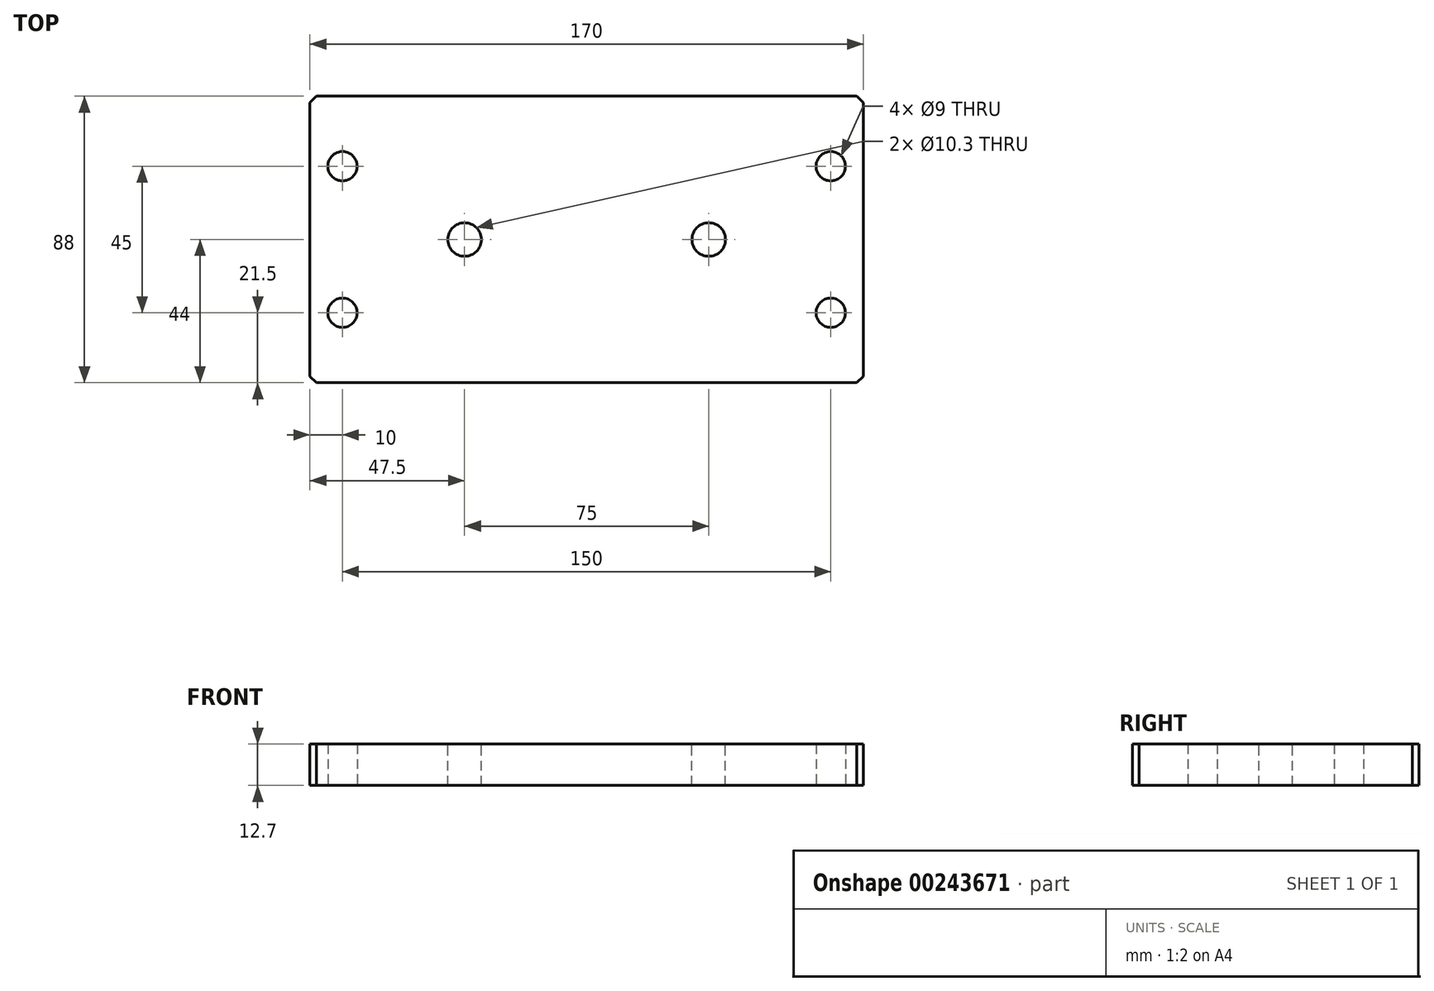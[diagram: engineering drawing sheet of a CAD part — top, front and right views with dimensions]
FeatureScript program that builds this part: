
annotation { "Feature Type Name" : "Feature", "Feature Type Description" : "" }
export const myFeature = defineFeature(function(context is Context, id is Id, definition is map)
    precondition{}
    {
        {
            var Q0;
            Q0=qCreatedBy(makeId("Top.planeOp"),FACE);
            var sketch = newSketch(context, id + "F0", { "sketchPlane" : qUnion([Q0])});
            skLineSegment(sketch, "E0.bottom", {"start": v(-85, -44) * mm, "end": v(85, -44) * mm});
            skLineSegment(sketch, "E0.top", {"start": v(-85, 44) * mm, "end": v(85, 44) * mm});
            skLineSegment(sketch, "E0.left", {"start": v(-85, -44) * mm, "end": v(-85, 44) * mm});
            skLineSegment(sketch, "E0.right", {"start": v(85, -44) * mm, "end": v(85, 44) * mm});
            skPoint(sketch, "E0.middle", {"position": v(0, 0) * mm});
            skLineSegment(sketch, "E1.bottom", {"start": v(-75, -22.5) * mm, "end": v(75, -22.5) * mm, "construction": true});
            skLineSegment(sketch, "E1.top", {"start": v(-75, 22.5) * mm, "end": v(75, 22.5) * mm, "construction": true});
            skLineSegment(sketch, "E1.left", {"start": v(-75, -22.5) * mm, "end": v(-75, 22.5) * mm, "construction": true});
            skLineSegment(sketch, "E1.right", {"start": v(75, -22.5) * mm, "end": v(75, 22.5) * mm, "construction": true});
            skCircle(sketch, "E2", {"center": v(-75, 22.5) * mm, "radius": 4.5 * mm});
            skCircle(sketch, "E3", {"center": v(75, 22.5) * mm, "radius": 4.5 * mm});
            skCircle(sketch, "E4", {"center": v(75, -22.5) * mm, "radius": 4.5 * mm});
            skCircle(sketch, "E5", {"center": v(-75, -22.5) * mm, "radius": 4.5 * mm});
            skSolve(sketch);
        }
        {
            var Q0;
            Q0 = qSketchRegion(id + "F0", true);
            extrude(context, id + "F1", {"entities" : qUnion([Q0]), "endBound" : BoundingType.SYMMETRIC, "depth" : 12.7 * mm});
        }
        {
            var Q0;
            Q0=makeQuery(id+"F1.opExtrude","SWEPT_EDGE",EDGE,{"disambiguationData":[OSD([sQuery(id+"F0.wireOp",EDGE,"E0.top"),sQuery(id+"F0.wireOp",EDGE,"E0.right")])]});
            var Q1;
            Q1=makeQuery(id+"F1.opExtrude","SWEPT_EDGE",EDGE,{"disambiguationData":[OSD([sQuery(id+"F0.wireOp",EDGE,"E0.bottom"),sQuery(id+"F0.wireOp",EDGE,"E0.right")])]});
            var Q2;
            Q2=makeQuery(id+"F1.opExtrude","SWEPT_EDGE",EDGE,{"disambiguationData":[OSD([sQuery(id+"F0.wireOp",EDGE,"E0.top"),sQuery(id+"F0.wireOp",EDGE,"E0.left")])]});
            var Q3;
            Q3=makeQuery(id+"F1.opExtrude","SWEPT_EDGE",EDGE,{"disambiguationData":[OSD([sQuery(id+"F0.wireOp",EDGE,"E0.bottom"),sQuery(id+"F0.wireOp",EDGE,"E0.left")])]});
            chamfer(context, id + "F2", {"entities" : qUnion([Q0, Q1, Q2, Q3]), "width" : 2 * mm, "tangentPropagation" : true});
        }
        {
            var Q0;
            Q0=makeQuery(id+"F1.opExtrude","CAP_FACE",FACE,{"disambiguationData":[OSD([sQuery(id+"F0.wireOp",EDGE,"E0.bottom"),sQuery(id+"F0.wireOp",EDGE,"E0.top"),sQuery(id+"F0.wireOp",EDGE,"E0.left"),sQuery(id+"F0.wireOp",EDGE,"E0.right"),sQuery(id+"F0.wireOp",EDGE,"E2"),sQuery(id+"F0.wireOp",EDGE,"E3"),sQuery(id+"F0.wireOp",EDGE,"E4"),sQuery(id+"F0.wireOp",EDGE,"E5")])],"isStart":false});
            var sketch = newSketch(context, id + "F3", { "sketchPlane" : qUnion([Q0])});
            skLineSegment(sketch, "E6", {"start": v(-37.5, 0) * mm, "end": v(37.5, 0) * mm, "construction": true});
            skSolve(sketch);
        }
        {
            var Q0;
            Q0=sQuery(id+"F3.wireOp",VERTEX,"E6.start");
            var Q1;
            Q1=sQuery(id+"F3.wireOp",VERTEX,"E6.end");
            var Q2;
            Q2=makeQuery(id+"F1.opExtrude","SWEPT_BODY",BODY,{"disambiguationData":[OSD([sQuery(id+"F0.wireOp",EDGE,"E0.bottom"),sQuery(id+"F0.wireOp",EDGE,"E0.top"),sQuery(id+"F0.wireOp",EDGE,"E0.left"),sQuery(id+"F0.wireOp",EDGE,"E0.right"),sQuery(id+"F0.wireOp",EDGE,"E2"),sQuery(id+"F0.wireOp",EDGE,"E3"),sQuery(id+"F0.wireOp",EDGE,"E4"),sQuery(id+"F0.wireOp",EDGE,"E5")])]});
            hole(context, id + "F4", {"style" : HoleStyle.SIMPLE, "endStyle" : HoleEndStyle.THROUGH, "standardTappedOrClearance" : lookupTablePath({ "standard" : "ISO", "engagement" : "75%", "pitch" : "1.75 mm", "size" : "M12", "type" : "Tapped" }), "standardBlindInLast" : lookupTablePath({ "standard" : "ISO", "engagement" : "75%", "pitch" : "1.75 mm", "size" : "M12", "type" : "Tapped" }), "holeDiameter" : 10.3 * mm, "showTappedDepth" : true, "tappedDepth" : 12.7 * mm, "tapClearance" : 3, "locations" : qUnion([Q0, Q1]), "scope" : qUnion([Q2]), "majorDiameter" : 12 * mm});
        }
    });
